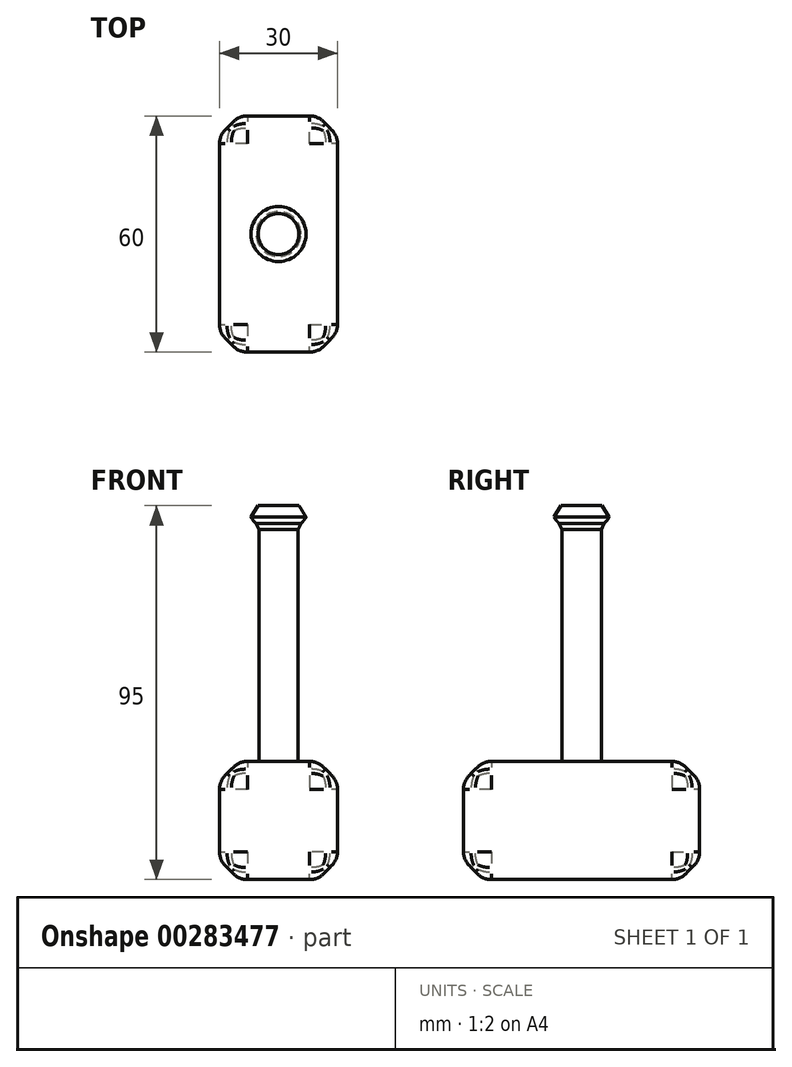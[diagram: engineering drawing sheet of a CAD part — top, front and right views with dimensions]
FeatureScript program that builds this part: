
annotation { "Feature Type Name" : "Feature", "Feature Type Description" : "" }
export const myFeature = defineFeature(function(context is Context, id is Id, definition is map)
    precondition{}
    {
        {
            var Q0;
            Q0=qCreatedBy(makeId("Top.planeOp"),FACE);
            var sketch = newSketch(context, id + "F0", { "sketchPlane" : qUnion([Q0])});
            skLineSegment(sketch, "E0.bottom", {"start": v(15, 30) * mm, "end": v(-15, 30) * mm});
            skLineSegment(sketch, "E0.top", {"start": v(15, -30) * mm, "end": v(-15, -30) * mm});
            skLineSegment(sketch, "E0.left", {"start": v(15, 30) * mm, "end": v(15, -30) * mm});
            skLineSegment(sketch, "E0.right", {"start": v(-15, 30) * mm, "end": v(-15, -30) * mm});
            skPoint(sketch, "E0.middle", {"position": v(0, 0) * mm});
            skSolve(sketch);
        }
        {
            var Q0;
            Q0=makeQuery(id+"F0.imprint","IMPRINT",FACE,{"disambiguationData":[TD([[makeQuery(id+"F0.imprint","IMPRINT",EDGE,{"derivedFrom":sQuery(id+"F0.wireOp",EDGE,"E0.bottom")}),1.0]])]});
            extrude(context, id + "F1", {"entities" : qUnion([Q0]), "depth" : 30 * mm});
        }
        {
            var Q0;
            Q0=makeQuery(id+"F1.opExtrude","CAP_FACE",FACE,{"disambiguationData":[OSD([sQuery(id+"F0.wireOp",EDGE,"E0.bottom"),sQuery(id+"F0.wireOp",EDGE,"E0.top"),sQuery(id+"F0.wireOp",EDGE,"E0.left"),sQuery(id+"F0.wireOp",EDGE,"E0.right")])],"isStart":false});
            var sketch = newSketch(context, id + "F2", { "sketchPlane" : qUnion([Q0])});
            skCircle(sketch, "E1", {"center": v(0, 0) * mm, "radius": 5 * mm});
            skSolve(sketch);
        }
        {
            var Q0;
            Q0=makeQuery(id+"F2.imprint","IMPRINT",FACE,{"disambiguationData":[TD([[makeQuery(id+"F2.imprint","IMPRINT",EDGE,{"derivedFrom":sQuery(id+"F2.wireOp",EDGE,"E1")}),1.0]])]});
            extrude(context, id + "F3", {"entities" : qUnion([Q0]), "operationType" : NewBodyOperationType.ADD, "depth" : 60 * mm});
        }
        {
            var Q0;
            Q0=makeQuery(id+"F3.opExtrude","CAP_FACE",FACE,{"disambiguationData":[OSD([sQuery(id+"F2.wireOp",EDGE,"E1")])],"isStart":false});
            var sketch = newSketch(context, id + "F4", { "sketchPlane" : qUnion([Q0])});
            skCircle(sketch, "E2", {"center": v(0, 0) * mm, "radius": 7.5 * mm});
            skSolve(sketch);
        }
        {
            var Q0;
            Q0=makeQuery(id+"F1.opExtrude","SWEPT_EDGE",EDGE,{"disambiguationData":[OSD([sQuery(id+"F0.wireOp",EDGE,"E0.bottom"),sQuery(id+"F0.wireOp",EDGE,"E0.right")])]});
            var Q1;
            Q1=makeQuery(id+"F1.opExtrude","SWEPT_EDGE",EDGE,{"disambiguationData":[OSD([sQuery(id+"F0.wireOp",EDGE,"E0.bottom"),sQuery(id+"F0.wireOp",EDGE,"E0.left")])]});
            var Q2;
            Q2=makeQuery(id+"F1.opExtrude","SWEPT_EDGE",EDGE,{"disambiguationData":[OSD([sQuery(id+"F0.wireOp",EDGE,"E0.top"),sQuery(id+"F0.wireOp",EDGE,"E0.left")])]});
            var Q3;
            Q3=makeQuery(id+"F1.opExtrude","SWEPT_EDGE",EDGE,{"disambiguationData":[OSD([sQuery(id+"F0.wireOp",EDGE,"E0.top"),sQuery(id+"F0.wireOp",EDGE,"E0.right")])]});
            var Q4;
            Q4=makeQuery(id+"F1.opExtrude","CAP_EDGE",EDGE,{"disambiguationData":[OSD([sQuery(id+"F0.wireOp",EDGE,"E0.right")])],"isStart":true});
            var Q5;
            Q5=makeQuery(id+"F1.opExtrude","CAP_EDGE",EDGE,{"disambiguationData":[OSD([sQuery(id+"F0.wireOp",EDGE,"E0.bottom")])],"isStart":true});
            var Q6;
            Q6=makeQuery(id+"F1.opExtrude","CAP_EDGE",EDGE,{"disambiguationData":[OSD([sQuery(id+"F0.wireOp",EDGE,"E0.left")])],"isStart":true});
            var Q7;
            Q7=makeQuery(id+"F1.opExtrude","CAP_EDGE",EDGE,{"disambiguationData":[OSD([sQuery(id+"F0.wireOp",EDGE,"E0.top")])],"isStart":true});
            var Q8;
            Q8=makeQuery(id+"F1.opExtrude","CAP_EDGE",EDGE,{"disambiguationData":[OSD([sQuery(id+"F0.wireOp",EDGE,"E0.right")])],"isStart":false});
            var Q9;
            Q9=makeQuery(id+"F1.opExtrude","CAP_EDGE",EDGE,{"disambiguationData":[OSD([sQuery(id+"F0.wireOp",EDGE,"E0.top")])],"isStart":false});
            var Q10;
            Q10=makeQuery(id+"F1.opExtrude","CAP_EDGE",EDGE,{"disambiguationData":[OSD([sQuery(id+"F0.wireOp",EDGE,"E0.left")])],"isStart":false});
            var Q11;
            Q11=makeQuery(id+"F1.opExtrude","CAP_EDGE",EDGE,{"disambiguationData":[OSD([sQuery(id+"F0.wireOp",EDGE,"E0.bottom")])],"isStart":false});
            chamfer(context, id + "F5", {"entities" : qUnion([Q0, Q1, Q2, Q3, Q4, Q5, Q6, Q7, Q8, Q9, Q10, Q11]), "width" : 5 * mm, "tangentPropagation" : true});
        }
        {
            var Q0;
            {var subQ0=sQuery(id+"F0.wireOp",EDGE,"E0.right");var subQ1=sQuery(id+"F0.wireOp",EDGE,"E0.top");Q0=makeQuery(id+"F5.opChamfer","BLEND_EDGE",EDGE,{"blendedFrom":[makeQuery(id+"F1.opExtrude","CAP_VERTEX",VERTEX,{"disambiguationData":[OSD([subQ1,subQ0])],"isStart":false}),makeQuery(id+"F1.opExtrude","SWEPT_EDGE",EDGE,{"disambiguationData":[OSD([subQ1,subQ0])]})],"blendedInto":[]});}
            var Q1;
            {var subQ0=sQuery(id+"F0.wireOp",EDGE,"E0.right");Q1=makeQuery(id+"F5.opChamfer","BLEND_EDGE",EDGE,{"blendedFrom":[makeQuery(id+"F1.opExtrude","CAP_VERTEX",VERTEX,{"disambiguationData":[OSD([sQuery(id+"F0.wireOp",EDGE,"E0.top"),subQ0])],"isStart":false}),makeQuery(id+"F1.opExtrude","CAP_EDGE",EDGE,{"disambiguationData":[OSD([subQ0])],"isStart":false})],"blendedInto":[]});}
            var Q2;
            {var subQ0=sQuery(id+"F0.wireOp",EDGE,"E0.right");Q2=makeQuery(id+"F5.opChamfer","BLEND_EDGE",EDGE,{"blendedFrom":[makeQuery(id+"F1.opExtrude","CAP_EDGE",EDGE,{"disambiguationData":[OSD([subQ0])],"isStart":false}),makeQuery(id+"F1.opExtrude","SWEPT_FACE",FACE,{"disambiguationData":[OSD([subQ0])]})],"blendedInto":[makeQuery(id+"F1.opExtrude","SWEPT_FACE",FACE,{"disambiguationData":[OSD([subQ0])]})]});}
            var Q3;
            {var subQ0=sQuery(id+"F0.wireOp",EDGE,"E0.right");Q3=makeQuery(id+"F5.opChamfer","BLEND_EDGE",EDGE,{"blendedFrom":[makeQuery(id+"F1.opExtrude","SWEPT_EDGE",EDGE,{"disambiguationData":[OSD([sQuery(id+"F0.wireOp",EDGE,"E0.top"),subQ0])]}),makeQuery(id+"F1.opExtrude","SWEPT_FACE",FACE,{"disambiguationData":[OSD([subQ0])]})],"blendedInto":[makeQuery(id+"F1.opExtrude","SWEPT_FACE",FACE,{"disambiguationData":[OSD([subQ0])]})]});}
            var Q4;
            {var subQ0=sQuery(id+"F0.wireOp",EDGE,"E0.right");Q4=makeQuery(id+"F5.opChamfer","BLEND_EDGE",EDGE,{"blendedFrom":[makeQuery(id+"F1.opExtrude","CAP_VERTEX",VERTEX,{"disambiguationData":[OSD([sQuery(id+"F0.wireOp",EDGE,"E0.bottom"),subQ0])],"isStart":false}),makeQuery(id+"F1.opExtrude","CAP_EDGE",EDGE,{"disambiguationData":[OSD([subQ0])],"isStart":false})],"blendedInto":[]});}
            var Q5;
            {var subQ0=sQuery(id+"F0.wireOp",EDGE,"E0.right");var subQ1=sQuery(id+"F0.wireOp",EDGE,"E0.bottom");Q5=makeQuery(id+"F5.opChamfer","BLEND_EDGE",EDGE,{"blendedFrom":[makeQuery(id+"F1.opExtrude","CAP_VERTEX",VERTEX,{"disambiguationData":[OSD([subQ1,subQ0])],"isStart":false}),makeQuery(id+"F1.opExtrude","SWEPT_EDGE",EDGE,{"disambiguationData":[OSD([subQ1,subQ0])]})],"blendedInto":[]});}
            var Q6;
            {var subQ0=sQuery(id+"F0.wireOp",EDGE,"E0.right");var subQ1=sQuery(id+"F0.wireOp",EDGE,"E0.bottom");Q6=makeQuery(id+"F5.opChamfer","BLEND_EDGE",EDGE,{"blendedFrom":[makeQuery(id+"F1.opExtrude","CAP_VERTEX",VERTEX,{"disambiguationData":[OSD([subQ1,subQ0])],"isStart":true}),makeQuery(id+"F1.opExtrude","SWEPT_EDGE",EDGE,{"disambiguationData":[OSD([subQ1,subQ0])]})],"blendedInto":[]});}
            var Q7;
            {var subQ0=sQuery(id+"F0.wireOp",EDGE,"E0.right");Q7=makeQuery(id+"F5.opChamfer","BLEND_EDGE",EDGE,{"blendedFrom":[makeQuery(id+"F1.opExtrude","CAP_VERTEX",VERTEX,{"disambiguationData":[OSD([sQuery(id+"F0.wireOp",EDGE,"E0.bottom"),subQ0])],"isStart":true}),makeQuery(id+"F1.opExtrude","CAP_EDGE",EDGE,{"disambiguationData":[OSD([subQ0])],"isStart":true})],"blendedInto":[]});}
            var Q8;
            {var subQ0=sQuery(id+"F0.wireOp",EDGE,"E0.right");Q8=makeQuery(id+"F5.opChamfer","BLEND_EDGE",EDGE,{"blendedFrom":[makeQuery(id+"F1.opExtrude","SWEPT_EDGE",EDGE,{"disambiguationData":[OSD([sQuery(id+"F0.wireOp",EDGE,"E0.bottom"),subQ0])]}),makeQuery(id+"F1.opExtrude","SWEPT_FACE",FACE,{"disambiguationData":[OSD([subQ0])]})],"blendedInto":[makeQuery(id+"F1.opExtrude","SWEPT_FACE",FACE,{"disambiguationData":[OSD([subQ0])]})]});}
            var Q9;
            {var subQ0=sQuery(id+"F0.wireOp",EDGE,"E0.right");Q9=makeQuery(id+"F5.opChamfer","BLEND_EDGE",EDGE,{"blendedFrom":[makeQuery(id+"F1.opExtrude","CAP_EDGE",EDGE,{"disambiguationData":[OSD([subQ0])],"isStart":true}),makeQuery(id+"F1.opExtrude","SWEPT_FACE",FACE,{"disambiguationData":[OSD([subQ0])]})],"blendedInto":[makeQuery(id+"F1.opExtrude","SWEPT_FACE",FACE,{"disambiguationData":[OSD([subQ0])]})]});}
            var Q10;
            {var subQ0=sQuery(id+"F0.wireOp",EDGE,"E0.right");var subQ1=sQuery(id+"F0.wireOp",EDGE,"E0.top");Q10=makeQuery(id+"F5.opChamfer","BLEND_EDGE",EDGE,{"blendedFrom":[makeQuery(id+"F1.opExtrude","CAP_VERTEX",VERTEX,{"disambiguationData":[OSD([subQ1,subQ0])],"isStart":true}),makeQuery(id+"F1.opExtrude","SWEPT_EDGE",EDGE,{"disambiguationData":[OSD([subQ1,subQ0])]})],"blendedInto":[]});}
            var Q11;
            {var subQ0=sQuery(id+"F0.wireOp",EDGE,"E0.right");Q11=makeQuery(id+"F5.opChamfer","BLEND_EDGE",EDGE,{"blendedFrom":[makeQuery(id+"F1.opExtrude","CAP_VERTEX",VERTEX,{"disambiguationData":[OSD([sQuery(id+"F0.wireOp",EDGE,"E0.top"),subQ0])],"isStart":true}),makeQuery(id+"F1.opExtrude","CAP_EDGE",EDGE,{"disambiguationData":[OSD([subQ0])],"isStart":true})],"blendedInto":[]});}
            var Q12;
            {var subQ0=sQuery(id+"F0.wireOp",EDGE,"E0.top");Q12=makeQuery(id+"F5.opChamfer","BLEND_EDGE",EDGE,{"blendedFrom":[makeQuery(id+"F1.opExtrude","CAP_EDGE",EDGE,{"disambiguationData":[OSD([subQ0])],"isStart":false}),makeQuery(id+"F1.opExtrude","CAP_FACE",FACE,{"disambiguationData":[OSD([sQuery(id+"F0.wireOp",EDGE,"E0.bottom"),subQ0,sQuery(id+"F0.wireOp",EDGE,"E0.left"),sQuery(id+"F0.wireOp",EDGE,"E0.right")])],"isStart":false})],"blendedInto":[makeQuery(id+"F1.opExtrude","CAP_FACE",FACE,{"disambiguationData":[OSD([sQuery(id+"F0.wireOp",EDGE,"E0.bottom"),subQ0,sQuery(id+"F0.wireOp",EDGE,"E0.left"),sQuery(id+"F0.wireOp",EDGE,"E0.right")])],"isStart":false})]});}
            var Q13;
            {var subQ0=sQuery(id+"F0.wireOp",EDGE,"E0.top");Q13=makeQuery(id+"F5.opChamfer","BLEND_EDGE",EDGE,{"blendedFrom":[makeQuery(id+"F1.opExtrude","CAP_EDGE",EDGE,{"disambiguationData":[OSD([subQ0])],"isStart":false}),makeQuery(id+"F1.opExtrude","SWEPT_FACE",FACE,{"disambiguationData":[OSD([subQ0])]})],"blendedInto":[makeQuery(id+"F1.opExtrude","SWEPT_FACE",FACE,{"disambiguationData":[OSD([subQ0])]})]});}
            var Q14;
            {var subQ0=sQuery(id+"F0.wireOp",EDGE,"E0.top");Q14=makeQuery(id+"F5.opChamfer","BLEND_EDGE",EDGE,{"blendedFrom":[makeQuery(id+"F1.opExtrude","SWEPT_EDGE",EDGE,{"disambiguationData":[OSD([subQ0,sQuery(id+"F0.wireOp",EDGE,"E0.right")])]}),makeQuery(id+"F1.opExtrude","SWEPT_FACE",FACE,{"disambiguationData":[OSD([subQ0])]})],"blendedInto":[makeQuery(id+"F1.opExtrude","SWEPT_FACE",FACE,{"disambiguationData":[OSD([subQ0])]})]});}
            var Q15;
            {var subQ0=sQuery(id+"F0.wireOp",EDGE,"E0.top");Q15=makeQuery(id+"F5.opChamfer","BLEND_EDGE",EDGE,{"blendedFrom":[makeQuery(id+"F1.opExtrude","CAP_EDGE",EDGE,{"disambiguationData":[OSD([subQ0])],"isStart":true}),makeQuery(id+"F1.opExtrude","SWEPT_FACE",FACE,{"disambiguationData":[OSD([subQ0])]})],"blendedInto":[makeQuery(id+"F1.opExtrude","SWEPT_FACE",FACE,{"disambiguationData":[OSD([subQ0])]})]});}
            var Q16;
            {var subQ0=sQuery(id+"F0.wireOp",EDGE,"E0.top");Q16=makeQuery(id+"F5.opChamfer","BLEND_EDGE",EDGE,{"blendedFrom":[makeQuery(id+"F1.opExtrude","CAP_EDGE",EDGE,{"disambiguationData":[OSD([subQ0])],"isStart":true}),makeQuery(id+"F1.opExtrude","CAP_FACE",FACE,{"disambiguationData":[OSD([sQuery(id+"F0.wireOp",EDGE,"E0.bottom"),subQ0,sQuery(id+"F0.wireOp",EDGE,"E0.left"),sQuery(id+"F0.wireOp",EDGE,"E0.right")])],"isStart":true})],"blendedInto":[makeQuery(id+"F1.opExtrude","CAP_FACE",FACE,{"disambiguationData":[OSD([sQuery(id+"F0.wireOp",EDGE,"E0.bottom"),subQ0,sQuery(id+"F0.wireOp",EDGE,"E0.left"),sQuery(id+"F0.wireOp",EDGE,"E0.right")])],"isStart":true})]});}
            var Q17;
            {var subQ0=sQuery(id+"F0.wireOp",EDGE,"E0.top");Q17=makeQuery(id+"F5.opChamfer","BLEND_EDGE",EDGE,{"blendedFrom":[makeQuery(id+"F1.opExtrude","CAP_VERTEX",VERTEX,{"disambiguationData":[OSD([subQ0,sQuery(id+"F0.wireOp",EDGE,"E0.right")])],"isStart":true}),makeQuery(id+"F1.opExtrude","CAP_EDGE",EDGE,{"disambiguationData":[OSD([subQ0])],"isStart":true})],"blendedInto":[]});}
            var Q18;
            {var subQ0=sQuery(id+"F0.wireOp",EDGE,"E0.top");Q18=makeQuery(id+"F5.opChamfer","BLEND_EDGE",EDGE,{"blendedFrom":[makeQuery(id+"F1.opExtrude","CAP_VERTEX",VERTEX,{"disambiguationData":[OSD([subQ0,sQuery(id+"F0.wireOp",EDGE,"E0.left")])],"isStart":true}),makeQuery(id+"F1.opExtrude","CAP_EDGE",EDGE,{"disambiguationData":[OSD([subQ0])],"isStart":true})],"blendedInto":[]});}
            var Q19;
            {var subQ0=sQuery(id+"F0.wireOp",EDGE,"E0.left");Q19=makeQuery(id+"F5.opChamfer","BLEND_EDGE",EDGE,{"blendedFrom":[makeQuery(id+"F1.opExtrude","CAP_VERTEX",VERTEX,{"disambiguationData":[OSD([sQuery(id+"F0.wireOp",EDGE,"E0.top"),subQ0])],"isStart":true}),makeQuery(id+"F1.opExtrude","CAP_EDGE",EDGE,{"disambiguationData":[OSD([subQ0])],"isStart":true})],"blendedInto":[]});}
            var Q20;
            {var subQ0=sQuery(id+"F0.wireOp",EDGE,"E0.left");var subQ1=sQuery(id+"F0.wireOp",EDGE,"E0.top");Q20=makeQuery(id+"F5.opChamfer","BLEND_EDGE",EDGE,{"blendedFrom":[makeQuery(id+"F1.opExtrude","CAP_VERTEX",VERTEX,{"disambiguationData":[OSD([subQ1,subQ0])],"isStart":false}),makeQuery(id+"F1.opExtrude","SWEPT_EDGE",EDGE,{"disambiguationData":[OSD([subQ1,subQ0])]})],"blendedInto":[]});}
            var Q21;
            {var subQ0=sQuery(id+"F0.wireOp",EDGE,"E0.left");var subQ1=sQuery(id+"F0.wireOp",EDGE,"E0.top");Q21=makeQuery(id+"F5.opChamfer","BLEND_EDGE",EDGE,{"blendedFrom":[makeQuery(id+"F1.opExtrude","CAP_VERTEX",VERTEX,{"disambiguationData":[OSD([subQ1,subQ0])],"isStart":true}),makeQuery(id+"F1.opExtrude","SWEPT_EDGE",EDGE,{"disambiguationData":[OSD([subQ1,subQ0])]})],"blendedInto":[]});}
            var Q22;
            {var subQ0=sQuery(id+"F0.wireOp",EDGE,"E0.top");Q22=makeQuery(id+"F5.opChamfer","BLEND_EDGE",EDGE,{"blendedFrom":[makeQuery(id+"F1.opExtrude","SWEPT_EDGE",EDGE,{"disambiguationData":[OSD([subQ0,sQuery(id+"F0.wireOp",EDGE,"E0.left")])]}),makeQuery(id+"F1.opExtrude","SWEPT_FACE",FACE,{"disambiguationData":[OSD([subQ0])]})],"blendedInto":[makeQuery(id+"F1.opExtrude","SWEPT_FACE",FACE,{"disambiguationData":[OSD([subQ0])]})]});}
            var Q23;
            {var subQ0=sQuery(id+"F0.wireOp",EDGE,"E0.left");Q23=makeQuery(id+"F5.opChamfer","BLEND_EDGE",EDGE,{"blendedFrom":[makeQuery(id+"F1.opExtrude","SWEPT_EDGE",EDGE,{"disambiguationData":[OSD([sQuery(id+"F0.wireOp",EDGE,"E0.top"),subQ0])]}),makeQuery(id+"F1.opExtrude","SWEPT_FACE",FACE,{"disambiguationData":[OSD([subQ0])]})],"blendedInto":[makeQuery(id+"F1.opExtrude","SWEPT_FACE",FACE,{"disambiguationData":[OSD([subQ0])]})]});}
            var Q24;
            {var subQ0=sQuery(id+"F0.wireOp",EDGE,"E0.top");Q24=makeQuery(id+"F5.opChamfer","BLEND_EDGE",EDGE,{"blendedFrom":[makeQuery(id+"F1.opExtrude","CAP_VERTEX",VERTEX,{"disambiguationData":[OSD([subQ0,sQuery(id+"F0.wireOp",EDGE,"E0.left")])],"isStart":false}),makeQuery(id+"F1.opExtrude","CAP_EDGE",EDGE,{"disambiguationData":[OSD([subQ0])],"isStart":false})],"blendedInto":[]});}
            var Q25;
            {var subQ0=sQuery(id+"F0.wireOp",EDGE,"E0.left");Q25=makeQuery(id+"F5.opChamfer","BLEND_EDGE",EDGE,{"blendedFrom":[makeQuery(id+"F1.opExtrude","CAP_VERTEX",VERTEX,{"disambiguationData":[OSD([sQuery(id+"F0.wireOp",EDGE,"E0.top"),subQ0])],"isStart":false}),makeQuery(id+"F1.opExtrude","CAP_EDGE",EDGE,{"disambiguationData":[OSD([subQ0])],"isStart":false})],"blendedInto":[]});}
            var Q26;
            {var subQ0=sQuery(id+"F0.wireOp",EDGE,"E0.left");Q26=makeQuery(id+"F5.opChamfer","BLEND_EDGE",EDGE,{"blendedFrom":[makeQuery(id+"F1.opExtrude","CAP_EDGE",EDGE,{"disambiguationData":[OSD([subQ0])],"isStart":false}),makeQuery(id+"F1.opExtrude","CAP_FACE",FACE,{"disambiguationData":[OSD([sQuery(id+"F0.wireOp",EDGE,"E0.bottom"),sQuery(id+"F0.wireOp",EDGE,"E0.top"),subQ0,sQuery(id+"F0.wireOp",EDGE,"E0.right")])],"isStart":false})],"blendedInto":[makeQuery(id+"F1.opExtrude","CAP_FACE",FACE,{"disambiguationData":[OSD([sQuery(id+"F0.wireOp",EDGE,"E0.bottom"),sQuery(id+"F0.wireOp",EDGE,"E0.top"),subQ0,sQuery(id+"F0.wireOp",EDGE,"E0.right")])],"isStart":false})]});}
            var Q27;
            {var subQ0=sQuery(id+"F0.wireOp",EDGE,"E0.left");Q27=makeQuery(id+"F5.opChamfer","BLEND_EDGE",EDGE,{"blendedFrom":[makeQuery(id+"F1.opExtrude","CAP_EDGE",EDGE,{"disambiguationData":[OSD([subQ0])],"isStart":false}),makeQuery(id+"F1.opExtrude","SWEPT_FACE",FACE,{"disambiguationData":[OSD([subQ0])]})],"blendedInto":[makeQuery(id+"F1.opExtrude","SWEPT_FACE",FACE,{"disambiguationData":[OSD([subQ0])]})]});}
            var Q28;
            {var subQ0=sQuery(id+"F0.wireOp",EDGE,"E0.left");Q28=makeQuery(id+"F5.opChamfer","BLEND_EDGE",EDGE,{"blendedFrom":[makeQuery(id+"F1.opExtrude","CAP_EDGE",EDGE,{"disambiguationData":[OSD([subQ0])],"isStart":true}),makeQuery(id+"F1.opExtrude","SWEPT_FACE",FACE,{"disambiguationData":[OSD([subQ0])]})],"blendedInto":[makeQuery(id+"F1.opExtrude","SWEPT_FACE",FACE,{"disambiguationData":[OSD([subQ0])]})]});}
            var Q29;
            {var subQ0=sQuery(id+"F0.wireOp",EDGE,"E0.left");Q29=makeQuery(id+"F5.opChamfer","BLEND_EDGE",EDGE,{"blendedFrom":[makeQuery(id+"F1.opExtrude","CAP_EDGE",EDGE,{"disambiguationData":[OSD([subQ0])],"isStart":true}),makeQuery(id+"F1.opExtrude","CAP_FACE",FACE,{"disambiguationData":[OSD([sQuery(id+"F0.wireOp",EDGE,"E0.bottom"),sQuery(id+"F0.wireOp",EDGE,"E0.top"),subQ0,sQuery(id+"F0.wireOp",EDGE,"E0.right")])],"isStart":true})],"blendedInto":[makeQuery(id+"F1.opExtrude","CAP_FACE",FACE,{"disambiguationData":[OSD([sQuery(id+"F0.wireOp",EDGE,"E0.bottom"),sQuery(id+"F0.wireOp",EDGE,"E0.top"),subQ0,sQuery(id+"F0.wireOp",EDGE,"E0.right")])],"isStart":true})]});}
            var Q30;
            {var subQ0=sQuery(id+"F0.wireOp",EDGE,"E0.bottom");Q30=makeQuery(id+"F5.opChamfer","BLEND_EDGE",EDGE,{"blendedFrom":[makeQuery(id+"F1.opExtrude","SWEPT_EDGE",EDGE,{"disambiguationData":[OSD([subQ0,sQuery(id+"F0.wireOp",EDGE,"E0.right")])]}),makeQuery(id+"F1.opExtrude","SWEPT_FACE",FACE,{"disambiguationData":[OSD([subQ0])]})],"blendedInto":[makeQuery(id+"F1.opExtrude","SWEPT_FACE",FACE,{"disambiguationData":[OSD([subQ0])]})]});}
            var Q31;
            {var subQ0=sQuery(id+"F0.wireOp",EDGE,"E0.bottom");Q31=makeQuery(id+"F5.opChamfer","BLEND_EDGE",EDGE,{"blendedFrom":[makeQuery(id+"F1.opExtrude","CAP_EDGE",EDGE,{"disambiguationData":[OSD([subQ0])],"isStart":true}),makeQuery(id+"F1.opExtrude","SWEPT_FACE",FACE,{"disambiguationData":[OSD([subQ0])]})],"blendedInto":[makeQuery(id+"F1.opExtrude","SWEPT_FACE",FACE,{"disambiguationData":[OSD([subQ0])]})]});}
            var Q32;
            {var subQ0=sQuery(id+"F0.wireOp",EDGE,"E0.bottom");Q32=makeQuery(id+"F5.opChamfer","BLEND_EDGE",EDGE,{"blendedFrom":[makeQuery(id+"F1.opExtrude","CAP_EDGE",EDGE,{"disambiguationData":[OSD([subQ0])],"isStart":false}),makeQuery(id+"F1.opExtrude","SWEPT_FACE",FACE,{"disambiguationData":[OSD([subQ0])]})],"blendedInto":[makeQuery(id+"F1.opExtrude","SWEPT_FACE",FACE,{"disambiguationData":[OSD([subQ0])]})]});}
            var Q33;
            {var subQ0=sQuery(id+"F0.wireOp",EDGE,"E0.bottom");Q33=makeQuery(id+"F5.opChamfer","BLEND_EDGE",EDGE,{"blendedFrom":[makeQuery(id+"F1.opExtrude","CAP_EDGE",EDGE,{"disambiguationData":[OSD([subQ0])],"isStart":false}),makeQuery(id+"F1.opExtrude","CAP_FACE",FACE,{"disambiguationData":[OSD([subQ0,sQuery(id+"F0.wireOp",EDGE,"E0.top"),sQuery(id+"F0.wireOp",EDGE,"E0.left"),sQuery(id+"F0.wireOp",EDGE,"E0.right")])],"isStart":false})],"blendedInto":[makeQuery(id+"F1.opExtrude","CAP_FACE",FACE,{"disambiguationData":[OSD([subQ0,sQuery(id+"F0.wireOp",EDGE,"E0.top"),sQuery(id+"F0.wireOp",EDGE,"E0.left"),sQuery(id+"F0.wireOp",EDGE,"E0.right")])],"isStart":false})]});}
            var Q34;
            {var subQ0=sQuery(id+"F0.wireOp",EDGE,"E0.bottom");Q34=makeQuery(id+"F5.opChamfer","BLEND_EDGE",EDGE,{"blendedFrom":[makeQuery(id+"F1.opExtrude","CAP_VERTEX",VERTEX,{"disambiguationData":[OSD([subQ0,sQuery(id+"F0.wireOp",EDGE,"E0.right")])],"isStart":false}),makeQuery(id+"F1.opExtrude","CAP_EDGE",EDGE,{"disambiguationData":[OSD([subQ0])],"isStart":false})],"blendedInto":[]});}
            var Q35;
            {var subQ0=sQuery(id+"F0.wireOp",EDGE,"E0.left");var subQ1=sQuery(id+"F0.wireOp",EDGE,"E0.bottom");Q35=makeQuery(id+"F5.opChamfer","BLEND_EDGE",EDGE,{"blendedFrom":[makeQuery(id+"F1.opExtrude","CAP_VERTEX",VERTEX,{"disambiguationData":[OSD([subQ1,subQ0])],"isStart":false}),makeQuery(id+"F1.opExtrude","SWEPT_EDGE",EDGE,{"disambiguationData":[OSD([subQ1,subQ0])]})],"blendedInto":[]});}
            var Q36;
            {var subQ0=sQuery(id+"F0.wireOp",EDGE,"E0.left");Q36=makeQuery(id+"F5.opChamfer","BLEND_EDGE",EDGE,{"blendedFrom":[makeQuery(id+"F1.opExtrude","CAP_VERTEX",VERTEX,{"disambiguationData":[OSD([sQuery(id+"F0.wireOp",EDGE,"E0.bottom"),subQ0])],"isStart":false}),makeQuery(id+"F1.opExtrude","CAP_EDGE",EDGE,{"disambiguationData":[OSD([subQ0])],"isStart":false})],"blendedInto":[]});}
            var Q37;
            {var subQ0=sQuery(id+"F0.wireOp",EDGE,"E0.left");var subQ1=sQuery(id+"F0.wireOp",EDGE,"E0.bottom");Q37=makeQuery(id+"F5.opChamfer","BLEND_EDGE",EDGE,{"blendedFrom":[makeQuery(id+"F1.opExtrude","CAP_VERTEX",VERTEX,{"disambiguationData":[OSD([subQ1,subQ0])],"isStart":true}),makeQuery(id+"F1.opExtrude","SWEPT_EDGE",EDGE,{"disambiguationData":[OSD([subQ1,subQ0])]})],"blendedInto":[]});}
            var Q38;
            {var subQ0=sQuery(id+"F0.wireOp",EDGE,"E0.left");Q38=makeQuery(id+"F5.opChamfer","BLEND_EDGE",EDGE,{"blendedFrom":[makeQuery(id+"F1.opExtrude","SWEPT_EDGE",EDGE,{"disambiguationData":[OSD([sQuery(id+"F0.wireOp",EDGE,"E0.bottom"),subQ0])]}),makeQuery(id+"F1.opExtrude","SWEPT_FACE",FACE,{"disambiguationData":[OSD([subQ0])]})],"blendedInto":[makeQuery(id+"F1.opExtrude","SWEPT_FACE",FACE,{"disambiguationData":[OSD([subQ0])]})]});}
            var Q39;
            {var subQ0=sQuery(id+"F0.wireOp",EDGE,"E0.bottom");Q39=makeQuery(id+"F5.opChamfer","BLEND_EDGE",EDGE,{"blendedFrom":[makeQuery(id+"F1.opExtrude","SWEPT_EDGE",EDGE,{"disambiguationData":[OSD([subQ0,sQuery(id+"F0.wireOp",EDGE,"E0.left")])]}),makeQuery(id+"F1.opExtrude","SWEPT_FACE",FACE,{"disambiguationData":[OSD([subQ0])]})],"blendedInto":[makeQuery(id+"F1.opExtrude","SWEPT_FACE",FACE,{"disambiguationData":[OSD([subQ0])]})]});}
            var Q40;
            {var subQ0=sQuery(id+"F0.wireOp",EDGE,"E0.bottom");Q40=makeQuery(id+"F5.opChamfer","BLEND_EDGE",EDGE,{"blendedFrom":[makeQuery(id+"F1.opExtrude","CAP_VERTEX",VERTEX,{"disambiguationData":[OSD([subQ0,sQuery(id+"F0.wireOp",EDGE,"E0.left")])],"isStart":false}),makeQuery(id+"F1.opExtrude","CAP_EDGE",EDGE,{"disambiguationData":[OSD([subQ0])],"isStart":false})],"blendedInto":[]});}
            var Q41;
            {var subQ0=sQuery(id+"F0.wireOp",EDGE,"E0.bottom");Q41=makeQuery(id+"F5.opChamfer","BLEND_EDGE",EDGE,{"blendedFrom":[makeQuery(id+"F1.opExtrude","CAP_VERTEX",VERTEX,{"disambiguationData":[OSD([subQ0,sQuery(id+"F0.wireOp",EDGE,"E0.left")])],"isStart":true}),makeQuery(id+"F1.opExtrude","CAP_EDGE",EDGE,{"disambiguationData":[OSD([subQ0])],"isStart":true})],"blendedInto":[]});}
            var Q42;
            {var subQ0=sQuery(id+"F0.wireOp",EDGE,"E0.left");Q42=makeQuery(id+"F5.opChamfer","BLEND_EDGE",EDGE,{"blendedFrom":[makeQuery(id+"F1.opExtrude","CAP_VERTEX",VERTEX,{"disambiguationData":[OSD([sQuery(id+"F0.wireOp",EDGE,"E0.bottom"),subQ0])],"isStart":true}),makeQuery(id+"F1.opExtrude","CAP_EDGE",EDGE,{"disambiguationData":[OSD([subQ0])],"isStart":true})],"blendedInto":[]});}
            var Q43;
            {var subQ0=sQuery(id+"F0.wireOp",EDGE,"E0.bottom");Q43=makeQuery(id+"F5.opChamfer","BLEND_EDGE",EDGE,{"blendedFrom":[makeQuery(id+"F1.opExtrude","CAP_VERTEX",VERTEX,{"disambiguationData":[OSD([subQ0,sQuery(id+"F0.wireOp",EDGE,"E0.right")])],"isStart":true}),makeQuery(id+"F1.opExtrude","CAP_EDGE",EDGE,{"disambiguationData":[OSD([subQ0])],"isStart":true})],"blendedInto":[]});}
            var Q44;
            {var subQ0=sQuery(id+"F0.wireOp",EDGE,"E0.right");Q44=makeQuery(id+"F5.opChamfer","BLEND_EDGE",EDGE,{"blendedFrom":[makeQuery(id+"F1.opExtrude","CAP_EDGE",EDGE,{"disambiguationData":[OSD([subQ0])],"isStart":true}),makeQuery(id+"F1.opExtrude","CAP_FACE",FACE,{"disambiguationData":[OSD([sQuery(id+"F0.wireOp",EDGE,"E0.bottom"),sQuery(id+"F0.wireOp",EDGE,"E0.top"),sQuery(id+"F0.wireOp",EDGE,"E0.left"),subQ0])],"isStart":true})],"blendedInto":[makeQuery(id+"F1.opExtrude","CAP_FACE",FACE,{"disambiguationData":[OSD([sQuery(id+"F0.wireOp",EDGE,"E0.bottom"),sQuery(id+"F0.wireOp",EDGE,"E0.top"),sQuery(id+"F0.wireOp",EDGE,"E0.left"),subQ0])],"isStart":true})]});}
            var Q45;
            {var subQ0=sQuery(id+"F0.wireOp",EDGE,"E0.bottom");Q45=makeQuery(id+"F5.opChamfer","BLEND_EDGE",EDGE,{"blendedFrom":[makeQuery(id+"F1.opExtrude","CAP_EDGE",EDGE,{"disambiguationData":[OSD([subQ0])],"isStart":true}),makeQuery(id+"F1.opExtrude","CAP_FACE",FACE,{"disambiguationData":[OSD([subQ0,sQuery(id+"F0.wireOp",EDGE,"E0.top"),sQuery(id+"F0.wireOp",EDGE,"E0.left"),sQuery(id+"F0.wireOp",EDGE,"E0.right")])],"isStart":true})],"blendedInto":[makeQuery(id+"F1.opExtrude","CAP_FACE",FACE,{"disambiguationData":[OSD([subQ0,sQuery(id+"F0.wireOp",EDGE,"E0.top"),sQuery(id+"F0.wireOp",EDGE,"E0.left"),sQuery(id+"F0.wireOp",EDGE,"E0.right")])],"isStart":true})]});}
            var Q46;
            {var subQ0=sQuery(id+"F0.wireOp",EDGE,"E0.right");Q46=makeQuery(id+"F5.opChamfer","BLEND_EDGE",EDGE,{"blendedFrom":[makeQuery(id+"F1.opExtrude","CAP_EDGE",EDGE,{"disambiguationData":[OSD([subQ0])],"isStart":false}),makeQuery(id+"F1.opExtrude","CAP_FACE",FACE,{"disambiguationData":[OSD([sQuery(id+"F0.wireOp",EDGE,"E0.bottom"),sQuery(id+"F0.wireOp",EDGE,"E0.top"),sQuery(id+"F0.wireOp",EDGE,"E0.left"),subQ0])],"isStart":false})],"blendedInto":[makeQuery(id+"F1.opExtrude","CAP_FACE",FACE,{"disambiguationData":[OSD([sQuery(id+"F0.wireOp",EDGE,"E0.bottom"),sQuery(id+"F0.wireOp",EDGE,"E0.top"),sQuery(id+"F0.wireOp",EDGE,"E0.left"),subQ0])],"isStart":false})]});}
            var Q47;
            {var subQ0=sQuery(id+"F0.wireOp",EDGE,"E0.top");Q47=makeQuery(id+"F5.opChamfer","BLEND_EDGE",EDGE,{"blendedFrom":[makeQuery(id+"F1.opExtrude","CAP_VERTEX",VERTEX,{"disambiguationData":[OSD([subQ0,sQuery(id+"F0.wireOp",EDGE,"E0.right")])],"isStart":false}),makeQuery(id+"F1.opExtrude","CAP_EDGE",EDGE,{"disambiguationData":[OSD([subQ0])],"isStart":false})],"blendedInto":[]});}
            fillet(context, id + "F6", {"entities" : qUnion([Q0, Q1, Q2, Q3, Q4, Q5, Q6, Q7, Q8, Q9, Q10, Q11, Q12, Q13, Q14, Q15, Q16, Q17, Q18, Q19, Q20, Q21, Q22, Q23, Q24, Q25, Q26, Q27, Q28, Q29, Q30, Q31, Q32, Q33, Q34, Q35, Q36, Q37, Q38, Q39, Q40, Q41, Q42, Q43, Q44, Q45, Q46, Q47]), "radius" : 5 * mm, "tangentPropagation" : true, "allowEdgeOverflow" : false});
        }
        {
            var Q0;
            Q0 = qSketchRegion(id + "F4", true);
            var Q1;
            Q1=makeQuery(id+"F4.imprint","IMPRINT",FACE,{"disambiguationData":[TD([[makeQuery(id+"F4.imprint","IMPRINT",EDGE,{"derivedFrom":sQuery(id+"F4.wireOp",EDGE,"E2")}),1.0]])]});
            extrude(context, id + "F7", {"entities" : qUnion([Q0, Q1]), "operationType" : NewBodyOperationType.ADD, "depth" : 5 * mm});
        }
        {
            var Q0;
            Q0=makeQuery(id+"F7.opExtrude","CAP_EDGE",EDGE,{"disambiguationData":[OSD([sQuery(id+"F4.wireOp",EDGE,"E2")])],"isStart":true});
            fillet(context, id + "F8", {"entities" : qUnion([Q0]), "radius" : 5 * mm, "tangentPropagation" : true, "allowEdgeOverflow" : false});
        }
        {
            var Q0;
            Q0=makeQuery(id+"F7.opExtrude","CAP_EDGE",EDGE,{"disambiguationData":[OSD([sQuery(id+"F4.wireOp",EDGE,"E2")])],"isStart":false});
            var Q1;
            Q1=makeQuery(id+"F8.opFillet","BLEND_FACE",FACE,{"disambiguationData":[OSD([sQuery(id+"F4.wireOp",EDGE,"E2")])]});
            chamfer(context, id + "F9", {"entities" : qUnion([Q0, Q1]), "width" : 2 * mm, "tangentPropagation" : true});
        }
    });
